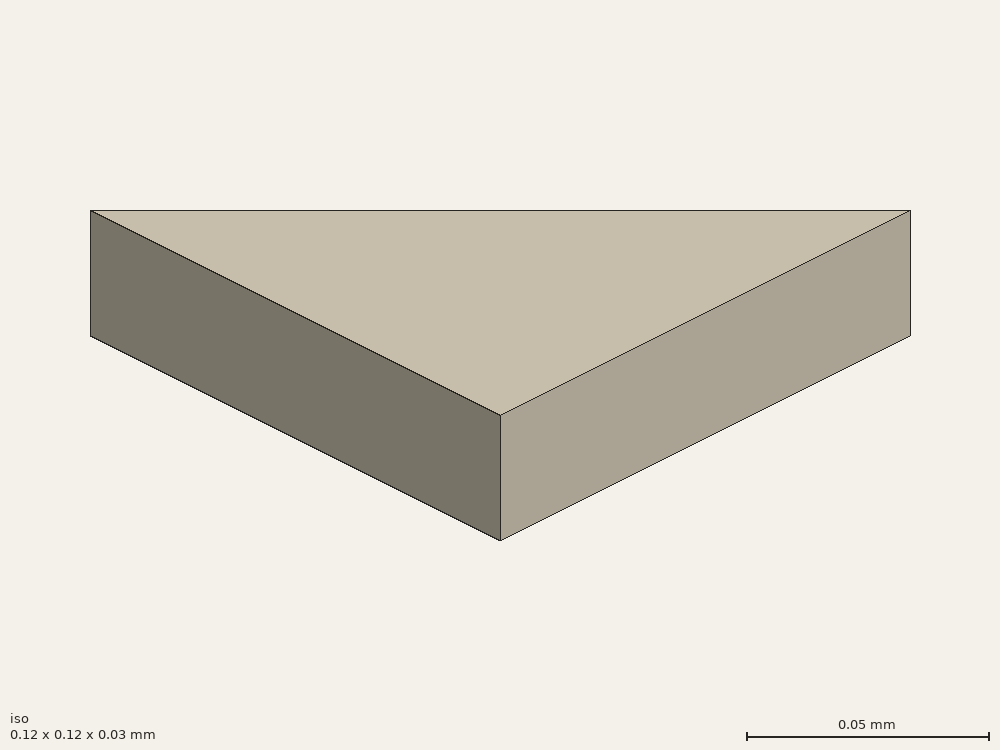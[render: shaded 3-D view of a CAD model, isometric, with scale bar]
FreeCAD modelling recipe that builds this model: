
FCSTD DOCUMENT  (FreeCAD 0.15R4671 (Git))
Label: triangle2
License: All rights reserved
LicenseURL: http://en.wikipedia.org/wiki/All_rights_reserved
objects: Sketcher::SketchObject×1, PartDesign::Pad×1
note: 3 computed .brp shape members not serialized (recipe doc carries the construction recipe); baked Part::Feature solids carry a one-line shape summary decoded from their .brp

FEATURE [Sketcher::SketchObject] Sketch
  sketch-geometry (3):
    g0: LineSegment StartX=-0.04 StartY=0.08 StartZ=0 EndX=-0.04 EndY=-0.04 EndZ=0
    g1: LineSegment StartX=-0.04 StartY=-0.04 StartZ=0 EndX=0.08 EndY=-0.04 EndZ=0
    g2: LineSegment StartX=0.08 StartY=-0.04 StartZ=0 EndX=-0.04 EndY=0.08 EndZ=0
  constraints (9):
    c: Coincident(g0,g1)
    c: Coincident(g1,g2)
    c: Coincident(g0,g2)
    c: Vertical(g0)
    c: DistanceY(g0) = -0.12
    c: Distance(g1,g0) = 0.12
    c: Distance(g-1,g0) = 0.04
    c: Perpendicular(g1,g0)
    c: Distance(g-1,g1) = 0.04
FEATURE [PartDesign::Pad] Pad
  Length = 0.03
  Length2 = 100
  Midplane = true
  Sketch = -> Sketch
  Type = 0
